# Revit family: ШУЗ
name_source: partatom
category: Оборудование
units: mm (PartAtom-declared; Revit-internal decimal feet)

## family parameters
Всегда вертикально = Да
Классификация = Нет
На основе рабочей плоскости = Нет
Общий = Нет
При загрузке вырезать с полостями = Нет
Размер круглого соединителя = Использовать диаметр
Тип детали = Нормальный
Точка расчета площади = Нет

## types (2) — shared parameters
URL = https://plazma-t.ru
Изготовитель = ООО "Плазма-Т"
Описание = ШУЗ-М предназначен для управления одно/трехфазным электроприводом задвижки практически любого производителя из известных на рынке. Управление осуществляется в режиме «Местный пуск» с лицевой панели ШУЗ-М или по сигналам любого модуля или прибора управления пожарного в режиме «Автоматический пуск» с отображением состояния задвижки при помощи световой индикации и с передачей сигналов состояния на модуль управления.
выход 3 = Да
zero-valued in all types: Отметка по умолчанию

## per-type parameters (varying)
| type | Комментарии к типоразмеру | Назв ПУШ | Расст ПУШ | Расст ввод | Расст ввод 2 | Расст замок | расст вывод |
| ШУЗ/IP31/DEK_ШУЗ/IP54/DEK | Ш1/DEK | 179 мм | 80 мм | 60 мм | 55 мм | 55 мм | 55 мм |
| ШУЗ/IP54/SE_ШУЗ/IP54/АВВ | Ш1/ABB | 120 мм | 30 мм | 220 мм | 100 мм | 260 мм | 100 мм |
